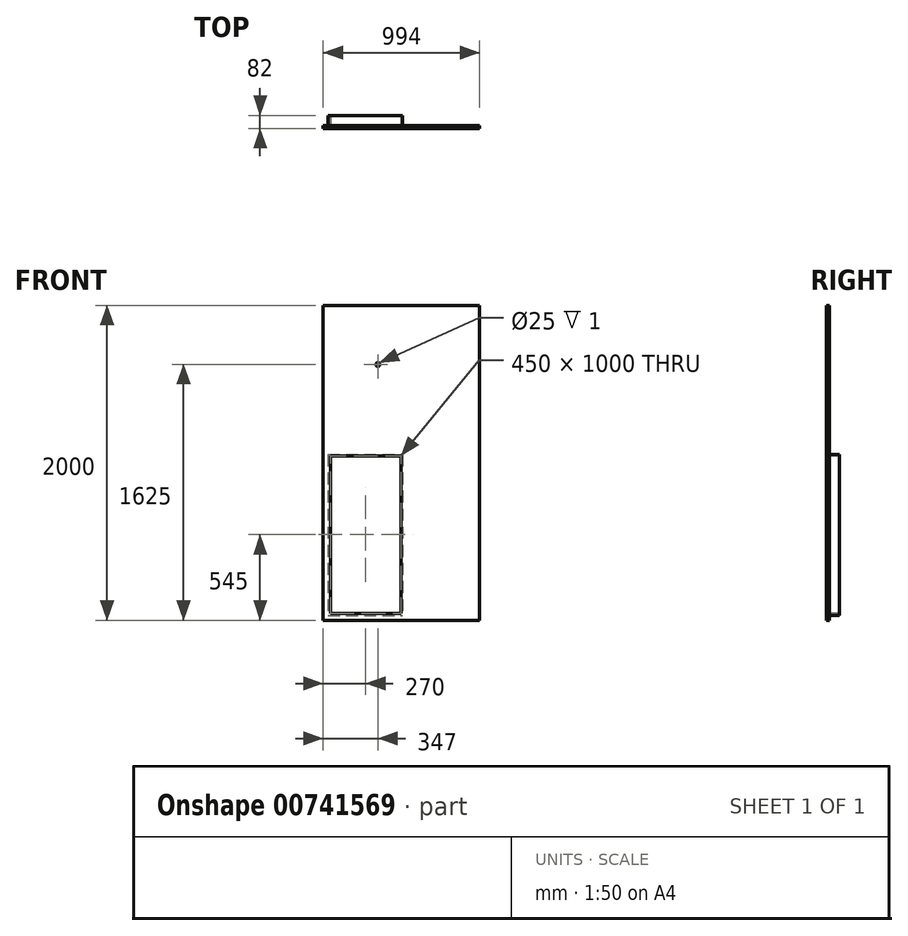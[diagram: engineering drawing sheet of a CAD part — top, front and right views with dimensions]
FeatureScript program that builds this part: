
annotation { "Feature Type Name" : "Feature", "Feature Type Description" : "" }
export const myFeature = defineFeature(function(context is Context, id is Id, definition is map)
    precondition{}
    {
        {
            var Q0;
            Q0=qCreatedBy(makeId("Front.planeOp"),FACE);
            var sketch = newSketch(context, id + "F0", { "sketchPlane" : qUnion([Q0])});
            skLineSegment(sketch, "E0.bottom", {"start": v(-497, -1000) * mm, "end": v(497, -1000) * mm});
            skLineSegment(sketch, "E0.top", {"start": v(-497, 1000) * mm, "end": v(497, 1000) * mm});
            skLineSegment(sketch, "E0.left", {"start": v(-497, -1000) * mm, "end": v(-497, 1000) * mm});
            skLineSegment(sketch, "E0.right", {"start": v(497, -1000) * mm, "end": v(497, 1000) * mm});
            skPoint(sketch, "E0.middle", {"position": v(0, 0) * mm});
            skSolve(sketch);
        }
        {
            var Q0;
            Q0=qSketchRegion(id+"F0",true);
            extrude(context, id + "F1", {"entities" : qUnion([Q0]), "oppositeDirection" : true, "depth" : 18 * mm, "offsetDistance" : 25 * mm});
        }
        {
            var Q0;
            Q0=makeQuery(id+"F1.opExtrude","CAP_FACE",FACE,{"disambiguationData":[OSD([sQuery(id+"F0.wireOp",EDGE,"E0.bottom"),sQuery(id+"F0.wireOp",EDGE,"E0.top"),sQuery(id+"F0.wireOp",EDGE,"E0.left"),sQuery(id+"F0.wireOp",EDGE,"E0.right")])],"isStart":true});
            var sketch = newSketch(context, id + "F2", { "sketchPlane" : qUnion([Q0])});
            skLineSegment(sketch, "E1", {"start": v(497, 625) * mm, "end": v(297, 625) * mm, "construction": true});
            skLineSegment(sketch, "E2", {"start": v(297, 625) * mm, "end": v(197, 625) * mm, "construction": true});
            skLineSegment(sketch, "E3", {"start": v(197, 625) * mm, "end": v(-497, 625) * mm, "construction": true});
            skCircle(sketch, "E4", {"center": v(-150, 625) * mm, "radius": 12.5 * mm});
            skSolve(sketch);
        }
        {
            var Q0;
            Q0=qSketchRegion(id+"F2",true);
            extrude(context, id + "F3", {"entities" : qUnion([Q0]), "operationType" : NewBodyOperationType.REMOVE, "oppositeDirection" : true, "depth" : 1 * mm, "offsetDistance" : 25 * mm});
        }
        {
            var Q0;
            Q0=makeQuery(id+"F1.opExtrude","CAP_FACE",FACE,{"disambiguationData":[OSD([sQuery(id+"F0.wireOp",EDGE,"E0.bottom"),sQuery(id+"F0.wireOp",EDGE,"E0.top"),sQuery(id+"F0.wireOp",EDGE,"E0.left"),sQuery(id+"F0.wireOp",EDGE,"E0.right")])],"isStart":true});
            var sketch = newSketch(context, id + "F4", { "sketchPlane" : qUnion([Q0])});
            skLineSegment(sketch, "E5.bottom", {"start": v(-452, -955) * mm, "end": v(-2, -955) * mm});
            skLineSegment(sketch, "E5.top", {"start": v(-452, 45) * mm, "end": v(-2, 45) * mm});
            skLineSegment(sketch, "E5.left", {"start": v(-452, -955) * mm, "end": v(-452, 45) * mm});
            skLineSegment(sketch, "E5.right", {"start": v(-2, -955) * mm, "end": v(-2, 45) * mm});
            skLineSegment(sketch, "E6", {"start": v(297, -1000) * mm, "end": v(297, 1000) * mm, "construction": true});
            skLineSegment(sketch, "E7", {"start": v(197, 1000) * mm, "end": v(197, -1000) * mm, "construction": true});
            skLineSegment(sketch, "E8", {"start": v(-227, -955) * mm, "end": v(-227, -1000) * mm, "construction": true});
            skLineSegment(sketch, "E9", {"start": v(-452, -455) * mm, "end": v(-497, -455) * mm, "construction": true});
            skSolve(sketch);
        }
        {
            var Q0;
            Q0=qSketchRegion(id+"F4",true);
            extrude(context, id + "F5", {"entities" : qUnion([Q0]), "operationType" : NewBodyOperationType.REMOVE, "oppositeDirection" : true, "depth" : 82 * mm, "offsetDistance" : 25 * mm});
        }
        {
            var Q0;
            Q0=makeQuery(id+"F1.opExtrude","CAP_FACE",FACE,{"disambiguationData":[OSD([sQuery(id+"F0.wireOp",EDGE,"E0.bottom"),sQuery(id+"F0.wireOp",EDGE,"E0.top"),sQuery(id+"F0.wireOp",EDGE,"E0.left"),sQuery(id+"F0.wireOp",EDGE,"E0.right")])],"isStart":true});
            var sketch = newSketch(context, id + "F6", { "sketchPlane" : qUnion([Q0])});
            skLineSegment(sketch, "E10.bottom", {"start": v(-465.32, 53.86) * mm, "end": v(5.74, 53.86) * mm});
            skLineSegment(sketch, "E10.top", {"start": v(-465.32, -969.06) * mm, "end": v(5.74, -969.06) * mm});
            skLineSegment(sketch, "E10.left", {"start": v(-465.32, 53.86) * mm, "end": v(-465.32, -969.06) * mm});
            skLineSegment(sketch, "E10.right", {"start": v(5.74, 53.86) * mm, "end": v(5.74, -969.06) * mm});
            skLineSegment(sketch, "E11.0", {"start": v(-452, -955) * mm, "end": v(-452, 45) * mm});
            skLineSegment(sketch, "E12.0", {"start": v(-452, -955) * mm, "end": v(-2, -955) * mm});
            skLineSegment(sketch, "E13.0", {"start": v(-2, -955) * mm, "end": v(-2, 45) * mm});
            skLineSegment(sketch, "E14.0", {"start": v(-452, 45) * mm, "end": v(-2, 45) * mm});
            skSolve(sketch);
        }
        {
            var Q0;
            Q0=makeQuery(id+"F6.imprint","IMPRINT",FACE,{"disambiguationData":[TD([[makeQuery(id+"F6.imprint","IMPRINT",EDGE,{"derivedFrom":sQuery(id+"F6.wireOp",EDGE,"E10.bottom")}),-1.0]])]});
            extrude(context, id + "F7", {"entities" : qUnion([Q0]), "operationType" : NewBodyOperationType.ADD, "oppositeDirection" : true, "depth" : 82 * mm, "offsetDistance" : 25 * mm});
        }
    });
